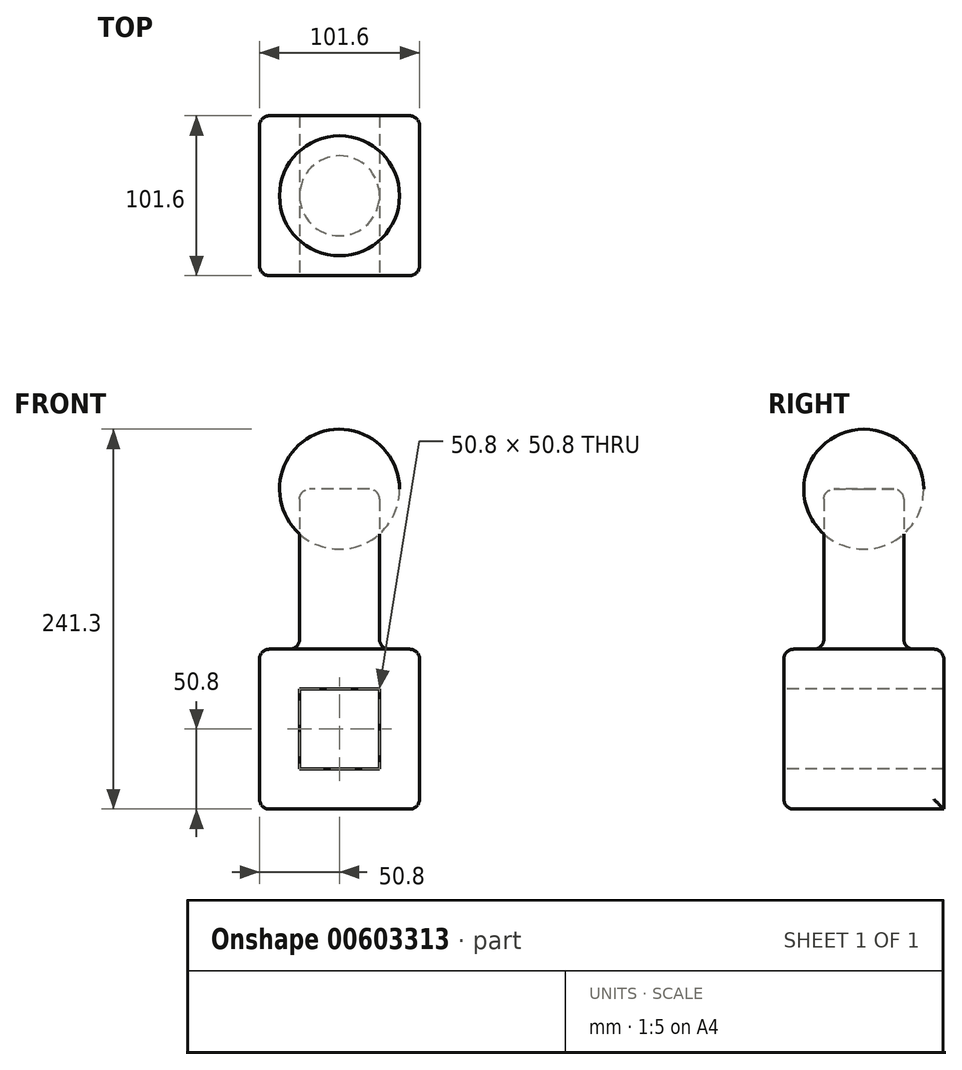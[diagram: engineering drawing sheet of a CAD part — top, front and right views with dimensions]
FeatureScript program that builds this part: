
annotation { "Feature Type Name" : "Feature", "Feature Type Description" : "" }
export const myFeature = defineFeature(function(context is Context, id is Id, definition is map)
    precondition{}
    {
        {
            var Q0;
            Q0=qCreatedBy(makeId("Top.planeOp"),FACE);
            var sketch = newSketch(context, id + "F0", { "sketchPlane" : qUnion([Q0])});
            skLineSegment(sketch, "E0.bottom", {"start": v(50.8, -50.8) * mm, "end": v(-50.8, -50.8) * mm});
            skLineSegment(sketch, "E0.top", {"start": v(50.8, 50.8) * mm, "end": v(-50.8, 50.8) * mm});
            skLineSegment(sketch, "E0.left", {"start": v(50.8, -50.8) * mm, "end": v(50.8, 50.8) * mm});
            skLineSegment(sketch, "E0.right", {"start": v(-50.8, -50.8) * mm, "end": v(-50.8, 50.8) * mm});
            skPoint(sketch, "E0.middle", {"position": v(0, 0) * mm});
            skSolve(sketch);
        }
        {
            var Q0;
            Q0 = qSketchRegion(id + "F0", true);
            extrude(context, id + "F1", {"entities" : qUnion([Q0]), "depth" : 101.6 * mm, "offsetDistance" : 25.4 * mm});
        }
        {
            var Q0;
            Q0=makeQuery(id+"F1.opExtrude","CAP_FACE",FACE,{"disambiguationData":[OSD([sQuery(id+"F0.wireOp",EDGE,"E0.bottom"),sQuery(id+"F0.wireOp",EDGE,"E0.top"),sQuery(id+"F0.wireOp",EDGE,"E0.left"),sQuery(id+"F0.wireOp",EDGE,"E0.right")])],"isStart":false});
            var sketch = newSketch(context, id + "F2", { "sketchPlane" : qUnion([Q0])});
            skSolve(sketch);
        }
        {
            var Q0;
            Q0=makeQuery(id+"F2.imprint","IMPRINT",FACE,{"disambiguationData":[TD([[makeQuery(id+"F2.imprint","IMPRINT",EDGE,{"derivedFrom":makeQuery(id+"F1.opExtrude","CAP_EDGE",EDGE,{"disambiguationData":[OSD([sQuery(id+"F0.wireOp",EDGE,"E0.bottom")])],"isStart":false})}),-1.0]])]});
            var sketch = newSketch(context, id + "F3", { "sketchPlane" : qUnion([Q0])});
            skCircle(sketch, "E1", {"center": v(0, 0) * mm, "radius": 25.4 * mm});
            skSolve(sketch);
        }
        {
            var Q0;
            Q0=makeQuery(id+"F3.imprint","IMPRINT",FACE,{"disambiguationData":[TD([[makeQuery(id+"F3.imprint","IMPRINT",EDGE,{"derivedFrom":sQuery(id+"F3.wireOp",EDGE,"E1")}),1.0]])]});
            extrude(context, id + "F4", {"entities" : qUnion([Q0]), "operationType" : NewBodyOperationType.ADD, "depth" : 101.6 * mm, "offsetDistance" : 25.4 * mm});
        }
        {
            var Q0;
            Q0=makeQuery(id+"F4.opExtrude","CAP_FACE",FACE,{"disambiguationData":[OSD([sQuery(id+"F3.wireOp",EDGE,"E1")])],"isStart":false});
            var sketch = newSketch(context, id + "F5", { "sketchPlane" : qUnion([Q0])});
            skArc(sketch, "E2", {"start": v(0, -38.1) * mm, "mid": v(38.1, 0) * mm, "end": v(0, 38.1) * mm});
            skLineSegment(sketch, "E3", {"start": v(0, 38.1) * mm, "end": v(0, -38.1) * mm});
            skSolve(sketch);
        }
        {
            var Q0;
            {var subQ0=sQuery(id+"F5.wireOp",EDGE,"E2");Q0=makeQuery(id+"F5.imprint","IMPRINT",FACE,{"disambiguationData":[TD([[makeQuery(id+"F5.imprint","IMPRINT",EDGE,{"derivedFrom":subQ0}),1.0]])]});}
            var Q1;
            {var subQ0=sQuery(id+"F5.wireOp",EDGE,"E3");var subQ1=makeQuery(id+"F4.opExtrude","CAP_EDGE",EDGE,{"disambiguationData":[OSD([sQuery(id+"F3.wireOp",EDGE,"E1")])],"isStart":false});var subQ2=makeQuery(id+"F5.imprint","INTERSECT",VERTEX,{"disambiguationData":[OD(0.0)],"derivedFrom":[subQ1,subQ0]});Q1=makeQuery(id+"F5.imprint","IMPRINT",FACE,{"disambiguationData":[TD([[makeQuery(id+"F5.imprint","IMPRINT",EDGE,{"disambiguationData":[TD([[subQ2,-1.0]])],"derivedFrom":subQ0}),1.0]])]});}
            var Q2;
            Q2=sQuery(id+"F5.wireOp",EDGE,"E3");
            revolve(context, id + "F6", {"entities" : qUnion([Q0, Q1]), "axis" : qUnion([Q2]), "revolveType" : RevolveType.FULL});
        }
        {
            var Q0;
            Q0=makeQuery(id+"F1.opExtrude","SWEPT_FACE",FACE,{"disambiguationData":[OSD([sQuery(id+"F0.wireOp",EDGE,"E0.bottom")])]});
            var sketch = newSketch(context, id + "F7", { "sketchPlane" : qUnion([Q0])});
            skLineSegment(sketch, "E4.bottom", {"start": v(25.4, 25.4) * mm, "end": v(-25.4, 25.4) * mm});
            skLineSegment(sketch, "E4.top", {"start": v(25.4, 76.2) * mm, "end": v(-25.4, 76.2) * mm});
            skLineSegment(sketch, "E4.left", {"start": v(25.4, 25.4) * mm, "end": v(25.4, 76.2) * mm});
            skLineSegment(sketch, "E4.right", {"start": v(-25.4, 25.4) * mm, "end": v(-25.4, 76.2) * mm});
            skPoint(sketch, "E4.middle", {"position": v(0, 50.8) * mm});
            skPoint(sketch, "E4.middle.positionSnap0", {"position": v(50.8, 50.8) * mm});
            skPoint(sketch, "E4.centerSnap0", {"position": v(50.8, 50.8) * mm});
            skSolve(sketch);
        }
        {
            var Q0;
            Q0=makeQuery(id+"F7.imprint","IMPRINT",FACE,{"disambiguationData":[TD([[makeQuery(id+"F7.imprint","IMPRINT",EDGE,{"derivedFrom":sQuery(id+"F7.wireOp",EDGE,"E4.bottom")}),-1.0]])]});
            extrude(context, id + "F8", {"entities" : qUnion([Q0]), "operationType" : NewBodyOperationType.REMOVE, "oppositeDirection" : true, "depth" : 101.6 * mm, "offsetDistance" : 25.4 * mm});
        }
        {
            var Q0;
            Q0=makeQuery(id+"F1.opExtrude","CAP_EDGE",EDGE,{"disambiguationData":[OSD([sQuery(id+"F0.wireOp",EDGE,"E0.left")])],"isStart":false});
            var Q1;
            Q1=makeQuery(id+"F1.opExtrude","SWEPT_EDGE",EDGE,{"disambiguationData":[OSD([sQuery(id+"F0.wireOp",EDGE,"E0.bottom"),sQuery(id+"F0.wireOp",EDGE,"E0.left")])]});
            var Q2;
            Q2=makeQuery(id+"F1.opExtrude","SWEPT_FACE",FACE,{"disambiguationData":[OSD([sQuery(id+"F0.wireOp",EDGE,"E0.left")])]});
            var Q3;
            Q3=makeQuery(id+"F1.opExtrude","CAP_EDGE",EDGE,{"disambiguationData":[OSD([sQuery(id+"F0.wireOp",EDGE,"E0.bottom")])],"isStart":false});
            var Q4;
            Q4=makeQuery(id+"F1.opExtrude","SWEPT_EDGE",EDGE,{"disambiguationData":[OSD([sQuery(id+"F0.wireOp",EDGE,"E0.bottom"),sQuery(id+"F0.wireOp",EDGE,"E0.right")])]});
            var Q5;
            Q5=makeQuery(id+"F1.opExtrude","CAP_EDGE",EDGE,{"disambiguationData":[OSD([sQuery(id+"F0.wireOp",EDGE,"E0.bottom")])],"isStart":true});
            var Q6;
            Q6=makeQuery(id+"F1.opExtrude","CAP_EDGE",EDGE,{"disambiguationData":[OSD([sQuery(id+"F0.wireOp",EDGE,"E0.right")])],"isStart":false});
            var Q7;
            Q7=makeQuery(id+"F1.opExtrude","CAP_EDGE",EDGE,{"disambiguationData":[OSD([sQuery(id+"F0.wireOp",EDGE,"E0.top")])],"isStart":false});
            var Q8;
            Q8=makeQuery(id+"F1.opExtrude","CAP_EDGE",EDGE,{"disambiguationData":[OSD([sQuery(id+"F0.wireOp",EDGE,"E0.right")])],"isStart":true});
            var Q9;
            Q9=makeQuery(id+"F1.opExtrude","SWEPT_EDGE",EDGE,{"disambiguationData":[OSD([sQuery(id+"F0.wireOp",EDGE,"E0.top"),sQuery(id+"F0.wireOp",EDGE,"E0.right")])]});
            var Q10;
            Q10=makeQuery(id+"F4.opExtrude","CAP_EDGE",EDGE,{"disambiguationData":[OSD([sQuery(id+"F3.wireOp",EDGE,"E1")])],"isStart":true});
            var Q11;
            Q11=makeQuery(id+"F4.opExtrude","SWEPT_FACE",FACE,{"disambiguationData":[OSD([sQuery(id+"F3.wireOp",EDGE,"E1")])]});
            fillet(context, id + "F9", {"entities" : qUnion([Q0, Q1, Q2, Q3, Q4, Q5, Q6, Q7, Q8, Q9, Q10, Q11]), "radius" : 6.35 * mm, "tangentPropagation" : true, "allowEdgeOverflow" : false});
        }
    });
